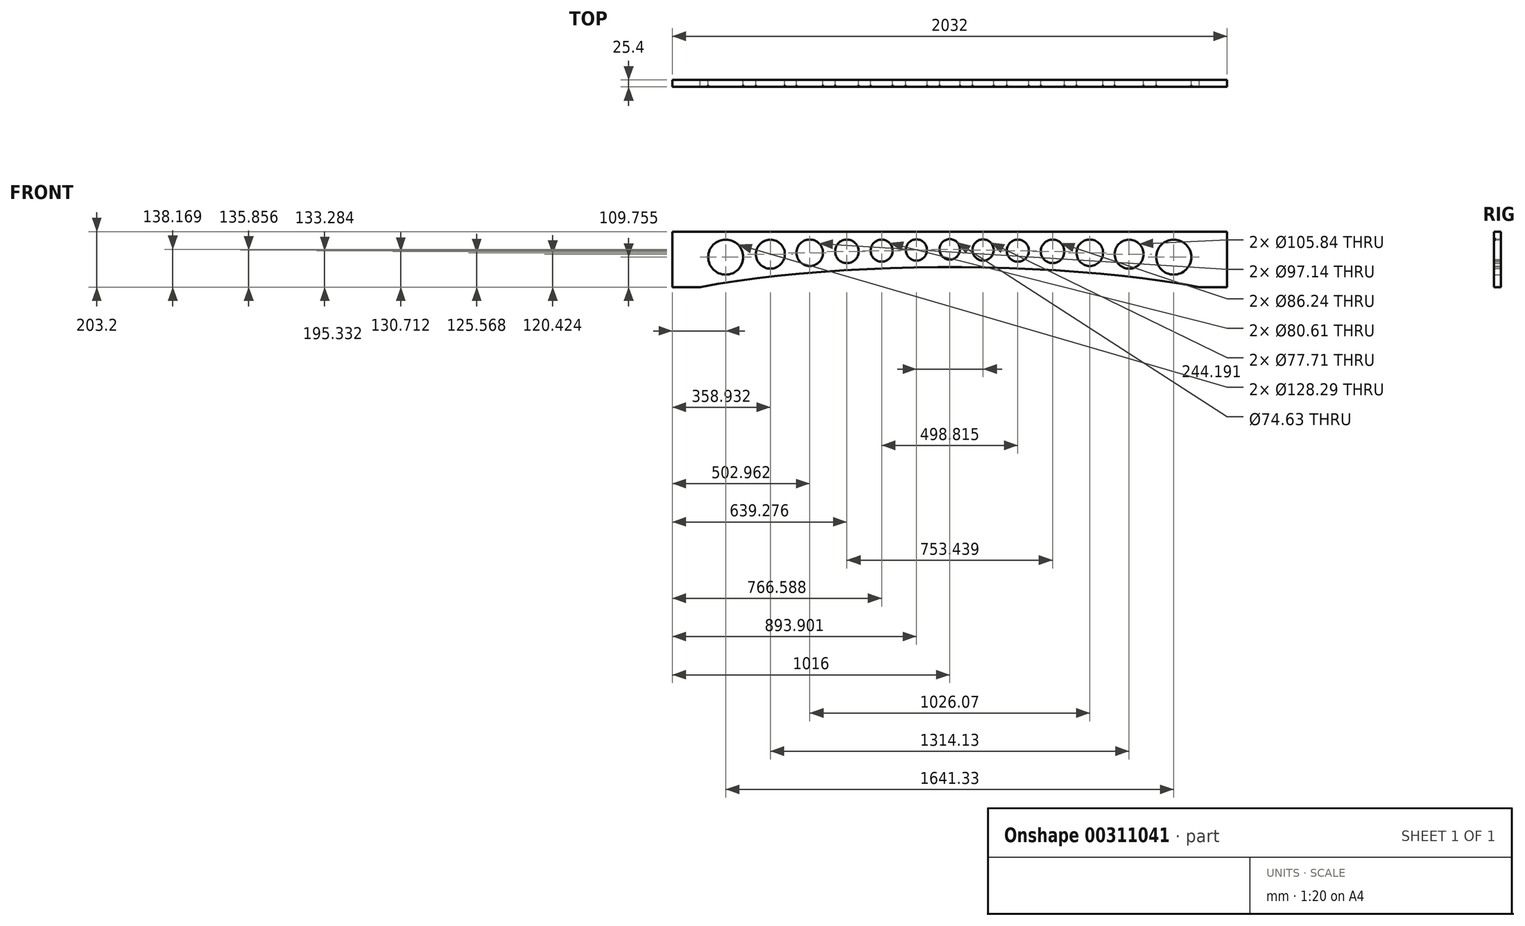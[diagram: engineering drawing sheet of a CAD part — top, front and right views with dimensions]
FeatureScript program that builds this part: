
annotation { "Feature Type Name" : "Feature", "Feature Type Description" : "" }
export const myFeature = defineFeature(function(context is Context, id is Id, definition is map)
    precondition{}
    {
        {
            var Q0;
            Q0=qCreatedBy(makeId("Front.planeOp"),FACE);
            var sketch = newSketch(context, id + "F0", { "sketchPlane" : qUnion([Q0])});
            skLineSegment(sketch, "E0.top", {"start": v(-1100.07, 136) * mm, "end": v(931.93, 136) * mm});
            skLineSegment(sketch, "E0.left", {"start": v(-1100.07, -67.2) * mm, "end": v(-1100.07, 136) * mm});
            skLineSegment(sketch, "E0.right", {"start": v(931.93, -67.2) * mm, "end": v(931.93, 136) * mm});
            skLineSegment(sketch, "E1", {"start": v(-1100.07, -67.2) * mm, "end": v(-998.47, -67.2) * mm});
            skLineSegment(sketch, "E2", {"start": v(931.93, -67.2) * mm, "end": v(830.33, -67.2) * mm});
            skEllipticalArc(sketch, "E3", {});
            skLineSegment(sketch, "E4", {"start": v(-84.07, 5.94) * mm, "end": v(-84.07, 136) * mm, "construction": true});
            skLineSegment(sketch, "E5", {"start": v(-998.47, -67.2) * mm, "end": v(-998.47, 136) * mm, "construction": true});
            skLineSegment(sketch, "E6", {"start": v(830.33, -67.2) * mm, "end": v(830.33, 136) * mm, "construction": true});
            skCircle(sketch, "E7", {"center": v(-904.74, 42.55) * mm, "radius": 64.15 * mm});
            skCircle(sketch, "E8", {"center": v(-84.07, 70.97) * mm, "radius": 37.31 * mm});
            skCircle(sketch, "E9", {"center": v(-597.1, 58.37) * mm, "radius": 48.57 * mm});
            skCircle(sketch, "E10", {"center": v(-460.8, 63.51) * mm, "radius": 43.12 * mm});
            skCircle(sketch, "E11", {"center": v(-333.48, 66.08) * mm, "radius": 40.3 * mm});
            skCircle(sketch, "E12", {"center": v(-206.17, 68.66) * mm, "radius": 38.86 * mm});
            skCircle(sketch, "E13", {"center": v(-741.14, 53.22) * mm, "radius": 52.92 * mm});
            skCircle(sketch, "E14.MirrorC", {"center": v(38.02, 68.66) * mm, "radius": 38.86 * mm});
            skCircle(sketch, "E15.MirrorC", {"center": v(165.33, 66.08) * mm, "radius": 40.3 * mm});
            skCircle(sketch, "E16.MirrorC", {"center": v(292.65, 63.51) * mm, "radius": 43.12 * mm});
            skCircle(sketch, "E17.MirrorC", {"center": v(428.96, 58.37) * mm, "radius": 48.57 * mm});
            skCircle(sketch, "E18.MirrorC", {"center": v(572.99, 53.22) * mm, "radius": 52.92 * mm});
            skCircle(sketch, "E19.MirrorC", {"center": v(736.6, 42.55) * mm, "radius": 64.15 * mm});
            const initialGuessF0  = {"E3": [-0.0840739980340004, -0.26696950828828436, 1, 0, 1.3421538125872612, 0.2729062281249346, 0.8212687708496629, 2.32032388274013]};
            skSetInitialGuess(sketch, initialGuessF0);
            skSolve(sketch);
        }
        {
            var Q0;
            Q0=makeQuery(id+"F0.imprint","IMPRINT",FACE,{"disambiguationData":[TD([[makeQuery(id+"F0.imprint","IMPRINT",EDGE,{"derivedFrom":sQuery(id+"F0.wireOp",EDGE,"E0.top")}),-1.0]])]});
            extrude(context, id + "F1", {"entities" : qUnion([Q0]), "depth" : 25.4 * mm});
        }
        {
            var Q0;
            Q0=makeQuery(id+"F1.opExtrude","CAP_EDGE",EDGE,{"disambiguationData":[OSD([sQuery(id+"F0.wireOp",EDGE,"E7")])],"isStart":false});
            fillet(context, id + "F2", {"entities" : qUnion([Q0]), "radius" : 6.35 * mm, "tangentPropagation" : true, "allowEdgeOverflow" : false});
        }
        {
            var Q0;
            Q0=makeQuery(id+"F1.opExtrude","CAP_EDGE",EDGE,{"disambiguationData":[OSD([sQuery(id+"F0.wireOp",EDGE,"E13")])],"isStart":false});
            var Q1;
            Q1=makeQuery(id+"F1.opExtrude","CAP_EDGE",EDGE,{"disambiguationData":[OSD([sQuery(id+"F0.wireOp",EDGE,"E9")])],"isStart":false});
            var Q2;
            Q2=makeQuery(id+"F1.opExtrude","CAP_EDGE",EDGE,{"disambiguationData":[OSD([sQuery(id+"F0.wireOp",EDGE,"E10")])],"isStart":false});
            var Q3;
            Q3=makeQuery(id+"F1.opExtrude","CAP_EDGE",EDGE,{"disambiguationData":[OSD([sQuery(id+"F0.wireOp",EDGE,"E11")])],"isStart":false});
            var Q4;
            Q4=makeQuery(id+"F1.opExtrude","CAP_EDGE",EDGE,{"disambiguationData":[OSD([sQuery(id+"F0.wireOp",EDGE,"E12")])],"isStart":false});
            var Q5;
            Q5=makeQuery(id+"F1.opExtrude","CAP_EDGE",EDGE,{"disambiguationData":[OSD([sQuery(id+"F0.wireOp",EDGE,"E8")])],"isStart":false});
            var Q6;
            Q6=makeQuery(id+"F1.opExtrude","CAP_EDGE",EDGE,{"disambiguationData":[OSD([sQuery(id+"F0.wireOp",EDGE,"E14.MirrorC")])],"isStart":false});
            var Q7;
            Q7=makeQuery(id+"F1.opExtrude","CAP_EDGE",EDGE,{"disambiguationData":[OSD([sQuery(id+"F0.wireOp",EDGE,"E15.MirrorC")])],"isStart":false});
            var Q8;
            Q8=makeQuery(id+"F1.opExtrude","CAP_EDGE",EDGE,{"disambiguationData":[OSD([sQuery(id+"F0.wireOp",EDGE,"E16.MirrorC")])],"isStart":false});
            var Q9;
            Q9=makeQuery(id+"F1.opExtrude","CAP_EDGE",EDGE,{"disambiguationData":[OSD([sQuery(id+"F0.wireOp",EDGE,"E17.MirrorC")])],"isStart":false});
            var Q10;
            Q10=makeQuery(id+"F1.opExtrude","CAP_EDGE",EDGE,{"disambiguationData":[OSD([sQuery(id+"F0.wireOp",EDGE,"E18.MirrorC")])],"isStart":false});
            var Q11;
            Q11=makeQuery(id+"F1.opExtrude","CAP_EDGE",EDGE,{"disambiguationData":[OSD([sQuery(id+"F0.wireOp",EDGE,"E19.MirrorC")])],"isStart":false});
            fillet(context, id + "F3", {"entities" : qUnion([Q0, Q1, Q2, Q3, Q4, Q5, Q6, Q7, Q8, Q9, Q10, Q11]), "radius" : 6.35 * mm, "tangentPropagation" : true, "allowEdgeOverflow" : false});
        }
    });
